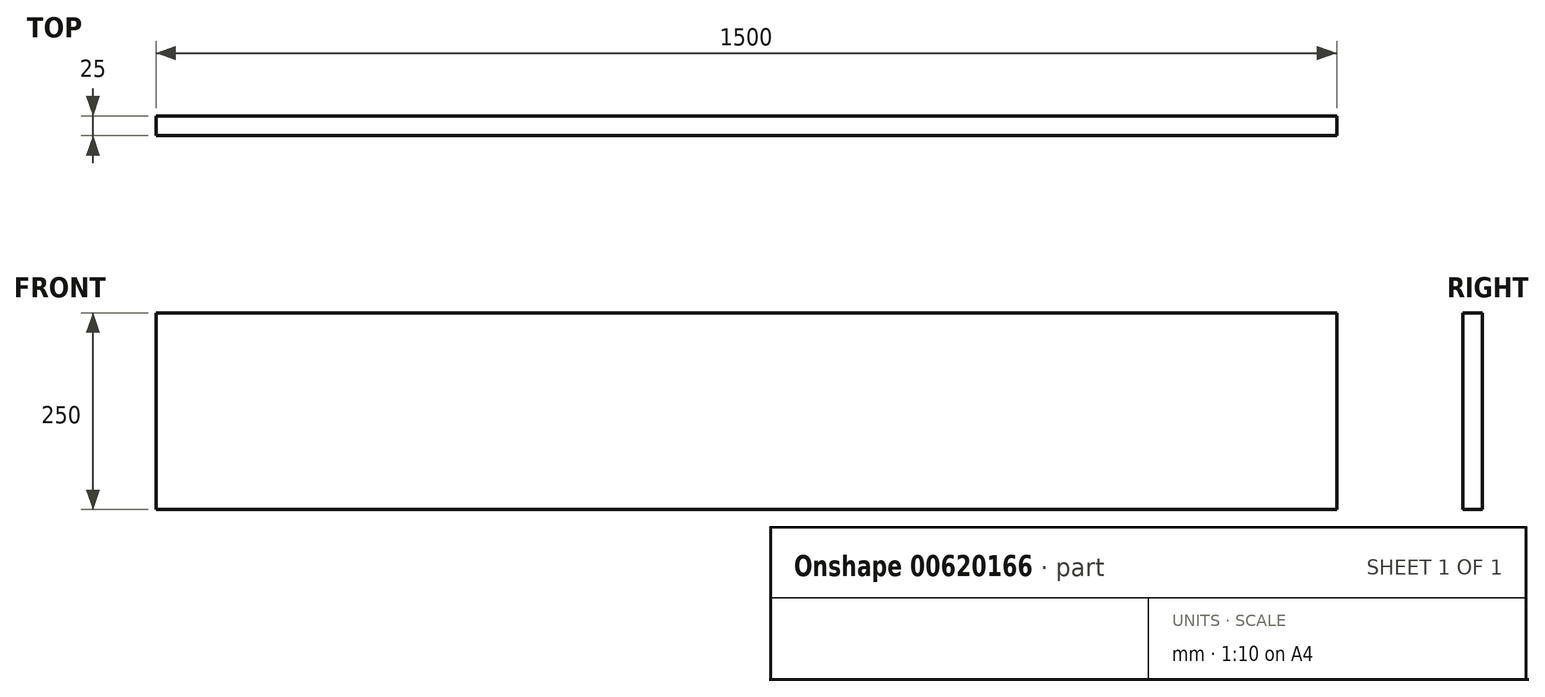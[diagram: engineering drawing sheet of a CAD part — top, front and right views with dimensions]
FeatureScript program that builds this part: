
annotation { "Feature Type Name" : "Feature", "Feature Type Description" : "" }
export const myFeature = defineFeature(function(context is Context, id is Id, definition is map)
    precondition{}
    {
        {
            var Q0;
            Q0=qCreatedBy(makeId("Front.planeOp"),FACE);
            var sketch = newSketch(context, id + "F0", { "sketchPlane" : qUnion([Q0])});
            skLineSegment(sketch, "E0.bottom", {"start": v(750, 125) * mm, "end": v(-750, 125) * mm});
            skLineSegment(sketch, "E0.top", {"start": v(750, -125) * mm, "end": v(-750, -125) * mm});
            skLineSegment(sketch, "E0.left", {"start": v(750, 125) * mm, "end": v(750, -125) * mm});
            skLineSegment(sketch, "E0.right", {"start": v(-750, 125) * mm, "end": v(-750, -125) * mm});
            skPoint(sketch, "E0.middle", {"position": v(0, 0) * mm});
            skSolve(sketch);
        }
        {
            var Q0;
            Q0=makeQuery(id+"F0.imprint","IMPRINT",FACE,{"disambiguationData":[TD([[makeQuery(id+"F0.imprint","IMPRINT",EDGE,{"derivedFrom":sQuery(id+"F0.wireOp",EDGE,"E0.bottom")}),1.0]])]});
            extrude(context, id + "F1", {"entities" : qUnion([Q0]), "depth" : 25 * mm, "offsetDistance" : 25 * mm});
        }
    });
